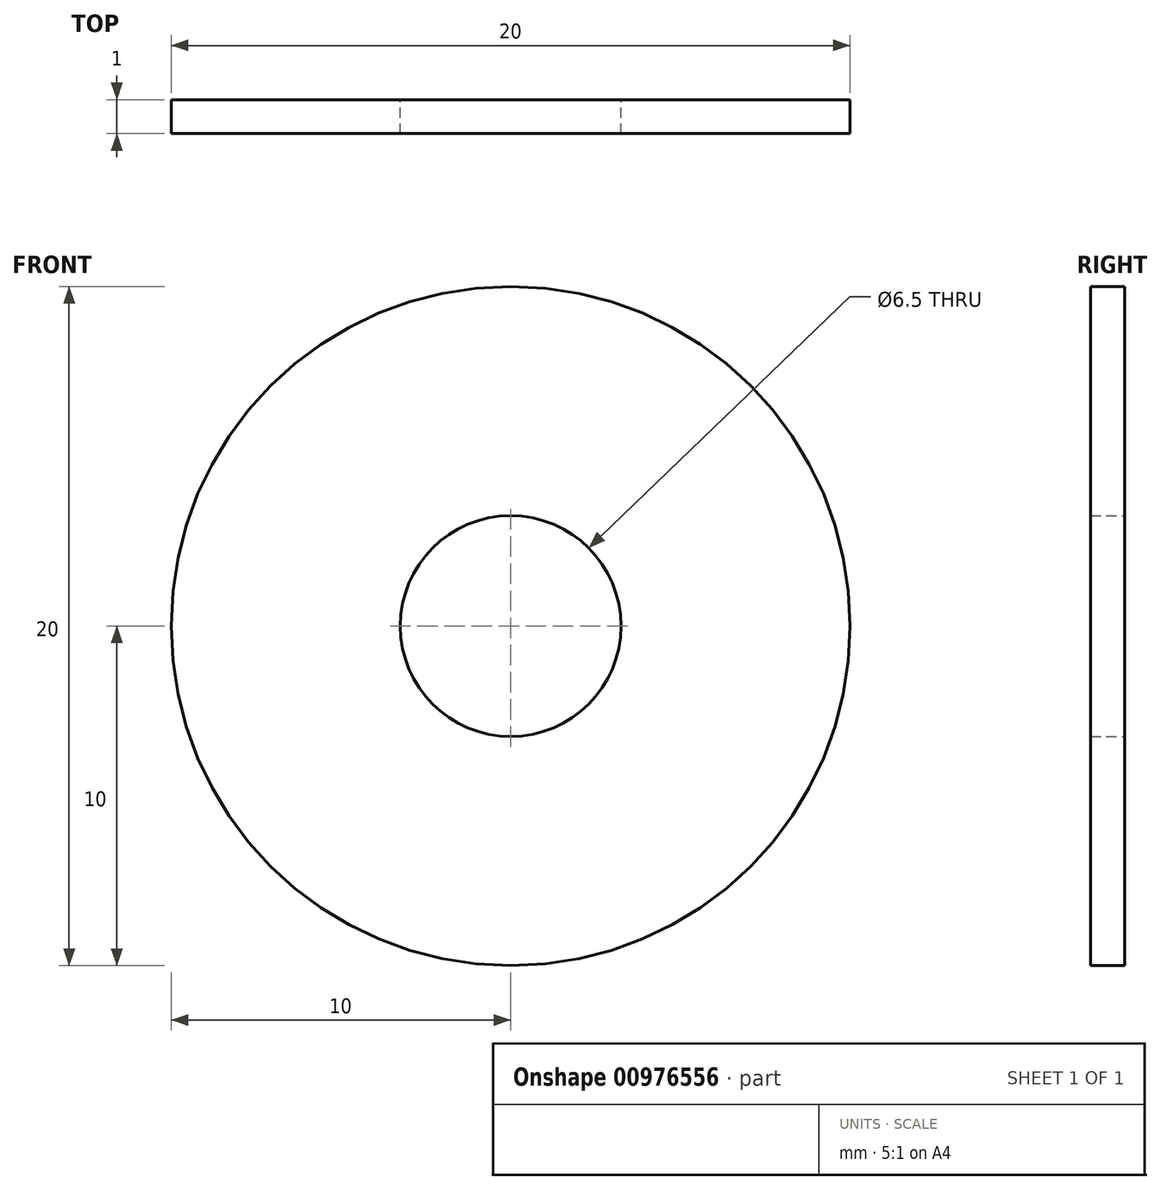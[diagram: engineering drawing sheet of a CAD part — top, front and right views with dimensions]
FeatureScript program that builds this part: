
annotation { "Feature Type Name" : "Feature", "Feature Type Description" : "" }
export const myFeature = defineFeature(function(context is Context, id is Id, definition is map)
    precondition{}
    {
        {
            var Q0;
            Q0=qCreatedBy(makeId("Front.planeOp"),FACE);
            var sketch = newSketch(context, id + "F0", { "sketchPlane" : qUnion([Q0])});
            skCircle(sketch, "E0", {"center": v(0, 0) * mm, "radius": 3.25 * mm});
            skCircle(sketch, "E1", {"center": v(0, 0) * mm, "radius": 10 * mm});
            skSolve(sketch);
        }
        {
            var Q0;
            Q0=makeQuery(id+"F0.imprint","IMPRINT",FACE,{"disambiguationData":[TD([[makeQuery(id+"F0.imprint","IMPRINT",EDGE,{"derivedFrom":sQuery(id+"F0.wireOp",EDGE,"E0")}),-1.0]])]});
            extrude(context, id + "F1", {"entities" : qUnion([Q0]), "depth" : 1 * mm, "offsetDistance" : 25 * mm});
        }
    });
